FCSTD DOCUMENT  (FreeCAD 0.20R29177 (Git))
Label: DonneesBoitier
License: All rights reserved
LicenseURL: http://en.wikipedia.org/wiki/All_rights_reserved
objects: Spreadsheet::Sheet×1

FEATURE [Spreadsheet::Sheet] Spreadsheet
  cells = A1=Angle; B1(xxAngle)=60; A2=LargEconche; B2(xxLargEconche)=15; A3=LongBase; B3(xxLongBase)=200; C3=Longeur de la base de l'enssemble , joue sur les angles et longeur de face Ar; A4=DiametreEcrou; B4(xxDiametreEcrou)=8; A5=AxeEncochesFaceAv; B5(xxAxeEncochesFaceAv)=10; C5=largeur de chaque cotés de l'ecran; D5=Sert à l'axe vertical du centre des trous et encoches en face AV; A6=EspaceTrouEncoche; B6(xxEspaceTrouEncoche)=15; A7=LargeurEncasEcran; B7(xxLargeurEncasEcran)=182; C7=Largeur encastrement ecran; D7=100; A8=HauteurEncasEcran; B8(xxHauteurEncasEcran)=263; C8=Hauteur encastrement ecran; D8=165; A9=EpaisseurEcran; B9(xxEpaisseurEcran)=24; A10=EpFaceAvAR; B10(xxEpFaceAvAr)=5; C10=Epaisseur Face Av AR; A11=EpEcrou; B11(xxEpEcrou)=4; C11=Epaisseur pour l'encastrement des ecrous; A12=DistEcrou; B12(xxDistEcrou)=5; C12=Distance d'encastrement de l'ecrou; A13=DiamVis; B13(xxDiamVis)=5; A14=LongVis; B14(xxLongVis)=12; A15=DiametreTrou; B15(xxDiametreTrou)==xxDiamVis * 1.05; C15=DiamVis + Marge 5%; A16=LargeurExtEcran; B16(xxLargeurExtEcran)=; C16=Largeur Externe de l'ecran; D16=110; A17=HauteurExtEcran; B17(xxHauteurExtEcran)=; C17=Hauteur Externe de l'ecran/ sert aussi pour la partie Ar rectiligne; D17=193; A18=RebordAvAr; B18(xxRebordAvAr)=10; C18=Rebord face Av et Ar par rapport au corp; D18=RebordAVAr+EpFaceAvAr/2 doit etre le centre de l'axe vertical sur lesquels sont centrés les trous et les encoches en facade; A19=FaEspaceHaut; B19(xxFaEspaceHaut)=35; C19=Espace entre le haut de la FA et le haut de l'ecran; A20=RapportHautEcranSurLarg; B20(xxRapportHautEcranSurLarg)=; C20=Pour garder un proportion du support; D20=xxHauteurExtEcran / xxLargeurExtEcran; A21=Hauteur; B21(xxHauteur)=380; C21=Hauteur Face AV; D21=xxHauteurExtEcran * xxRapportHautEcranSurLarg; E21=338.63; A22=Largeur; B22(xxlargeur)=220; C22=Largeur Face AV et AR 140 ecran encastrable AV ; D22=xxLargeurExtEcran + 2 * xxBordEcranFaceAv; E22=160; A23=EpEncoche; B23(xxEpEncoche)==xxEpFaceAvAr; C23=egal epaisseur face AvAr; A24=HautEncocheFemelle; B24(xxHautEncocheFemelle)==xxEpEncoche + 0.2; C24=EpEncoche + Marge si necessaire; D24=?? Hauteur encoche femelle; E24=xxEpTrou; A25=LargEncocheFemelle; B25(xxLargEncocheFemelle)==xxLargEconche + 0.2; C25=LargEconche + Marge de 10%; D25=?? Largeur encoche femelle; E25=xxLargTrou; A26=LongEncoches; B26(xxLongEncoches)==xxEpFaceAvAr; C26=egal epaisseur face AvAr; A27=RayonCongé; B27(xxRayonConge)=10; A28=LargLatHaut; B28(xxLargLatHaut)=65; C28=Largeur laterale et Largeur dessus totale sans encoche; A29=LongDessus; B29(xxLongDessus)==xxlargeur - 2 * xxAxeEncochesFaceAv - xxLongEncoches; A30=LongeurDecoupe; B30(xxLongeurDecoupe)=30; A31=LargeurDecoupe; B31(xxLargeurDecoupe)=2; A32=EspaceDecoupe; B32(xxEspaceDecoupe)=4; A33=SautLigneDecoupe; B33(xxSautLigneDecoupe)=3; A36=ArHautPartieHaute; B36(xxArHautPartieHaute)==xxHauteurEncasEcran; C36=Haute de la partie Ar non flexible; A37=Face Ar; A38=HauteurAr; B38(xxHauteurAr)==121.6 + 60 + 27.5 + 123.3 + xxRebordAvAr; C38=Mesure du coté dans Curve avec (I) + xxRebordAvAr; D38=121.6+60+27,5+123,3; A39=EspaceDebutCourbe; B39(xxEspaceDebutCourbe)=15; C39=Espace haut (  par rapport encoche)et bas du début et fin de la courbe mesuré sur proto; A40=EspaceFinCourbe; B40(xxEspaceFinCourbe)==xxEspaceDebutCourbe / 2; A41=DecoupeHauteur; B41(xxDecoupeHauteur)=128; C41=Mesure sur lignes de construction; A42=Vasa; B42(xxVesa)=75
